# Revit family: Hook_A10_EMCO
name_source: partatom
category: Generic Models
units: mm (PartAtom-declared; Revit-internal decimal feet)

## family parameters
Always vertical = Yes
Can host rebar = No
Cut with Voids When Loaded = Yes
Maintain Annotation Orientation = No
Part Type = Normal
Room Calculation Point = No
Round Connector Dimension = Use Diameter
Shared = No
Work Plane-Based = Yes

## types (1)
- Hook_A10_EMCO
    Assembly Code = E1090900
    Construction Details = http://emcospi.com
    Default Elevation = 4' - 0"
    Description = EMCO A10 Hat and Coat Hook
    Hook Material = EMCO  - Silver Finish
    Installation Phase = Closet and Utility Shelving Hardware
    Installation-Fabrication = http://emcospi.com
    Keynote = 10 57 33
    Manufacturer = EMCO Specialty Products, Inc.
    Manufacturer Fax = 913-281-4554
    Manufacturer Website = http://www.emcospi.com
    Model = EMCO A10 Hat and Coat Hook
    Product Data = http://emcospi.com
    Product Properties = http://www.arcat.com
    Sales Information = http://www.emcospi.com
    Send Message = http://www.emcospi.com
    URL = https://www.arcat.com
    Warranty Duration (Years) = 1

## geometry (parser evidence)
native form markers: Sweep x1
no freeform markers — native parametric forms only
